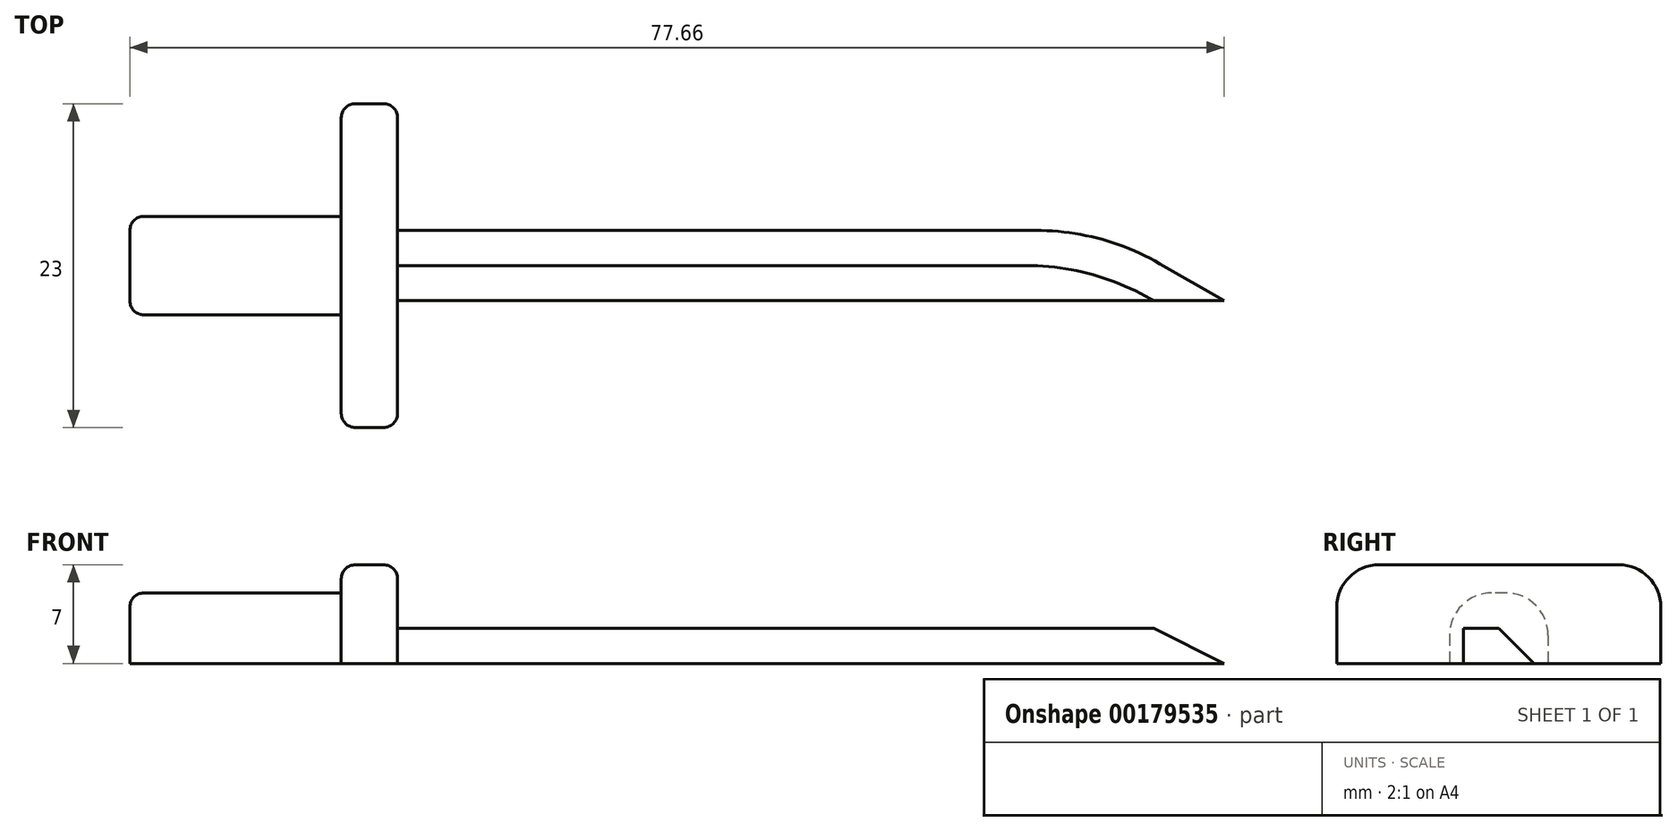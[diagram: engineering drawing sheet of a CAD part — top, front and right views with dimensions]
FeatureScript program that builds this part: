
annotation { "Feature Type Name" : "Feature", "Feature Type Description" : "" }
export const myFeature = defineFeature(function(context is Context, id is Id, definition is map)
    precondition{}
    {
        {
            var Q0;
            Q0=qCreatedBy(makeId("Top.planeOp"),FACE);
            var sketch = newSketch(context, id + "F0", { "sketchPlane" : qUnion([Q0])});
            skLineSegment(sketch, "E0.bottom", {"start": v(0, 0) * mm, "end": v(50, 0) * mm});
            skLineSegment(sketch, "E0.top", {"start": v(0, -5) * mm, "end": v(50, -5) * mm});
            skLineSegment(sketch, "E0.left", {"start": v(0, 0) * mm, "end": v(0, -5) * mm});
            skLineSegment(sketch, "E0.right", {"start": v(50, 0) * mm, "end": v(50, -5) * mm});
            skLineSegment(sketch, "E1", {"start": v(50, 0) * mm, "end": v(58.66, -5) * mm});
            skLineSegment(sketch, "E2", {"start": v(58.66, -5) * mm, "end": v(50, -5) * mm});
            skLineSegment(sketch, "E3.bottom", {"start": v(-4, 9) * mm, "end": v(0, 9) * mm});
            skLineSegment(sketch, "E3.top", {"start": v(-4, -14) * mm, "end": v(0, -14) * mm});
            skLineSegment(sketch, "E3.left", {"start": v(-4, 9) * mm, "end": v(-4, -14) * mm});
            skLineSegment(sketch, "E3.right", {"start": v(0, 9) * mm, "end": v(0, -14) * mm});
            skLineSegment(sketch, "E4.bottom", {"start": v(-19, 1) * mm, "end": v(-4, 1) * mm});
            skLineSegment(sketch, "E4.top", {"start": v(-19, -6) * mm, "end": v(-4, -6) * mm});
            skLineSegment(sketch, "E4.left", {"start": v(-19, 1) * mm, "end": v(-19, -6) * mm});
            skLineSegment(sketch, "E4.right", {"start": v(-4, 1) * mm, "end": v(-4, -6) * mm});
            skSolve(sketch);
        }
        {
            var Q0;
            {var subQ0=sQuery(id+"F0.wireOp",EDGE,"E0.bottom");Q0=makeQuery(id+"F0.imprint","IMPRINT",FACE,{"disambiguationData":[TD([[makeQuery(id+"F0.imprint","IMPRINT",EDGE,{"derivedFrom":subQ0}),-1.0]])]});}
            var Q1;
            Q1=makeQuery(id+"F0.imprint","IMPRINT",FACE,{"disambiguationData":[TD([[makeQuery(id+"F0.imprint","IMPRINT",EDGE,{"derivedFrom":sQuery(id+"F0.wireOp",EDGE,"E0.right")}),1.0]])]});
            extrude(context, id + "F1", {"entities" : qUnion([Q0, Q1]), "depth" : 2.5 * mm});
        }
        {
            var Q0;
            Q0=makeQuery(id+"F0.imprint","IMPRINT",FACE,{"disambiguationData":[TD([[makeQuery(id+"F0.imprint","IMPRINT",EDGE,{"derivedFrom":sQuery(id+"F0.wireOp",EDGE,"E4.bottom")}),-1.0]])]});
            extrude(context, id + "F2", {"entities" : qUnion([Q0]), "depth" : 5 * mm});
        }
        {
            var Q0;
            {var subQ3=sQuery(id+"F0.wireOp",EDGE,"E3.bottom");Q0=makeQuery(id+"F0.imprint","IMPRINT",FACE,{"disambiguationData":[TD([[makeQuery(id+"F0.imprint","IMPRINT",EDGE,{"derivedFrom":subQ3}),-1.0]])]});}
            extrude(context, id + "F3", {"entities" : qUnion([Q0]), "depth" : 7 * mm});
        }
        {
            var Q0;
            Q0=makeQuery(id+"F1.opExtrude","CAP_EDGE",EDGE,{"disambiguationData":[OSD([sQuery(id+"F0.wireOp",EDGE,"E0.bottom")])],"isStart":false});
            var Q1;
            Q1=makeQuery(id+"F1.opExtrude","CAP_EDGE",EDGE,{"disambiguationData":[OSD([sQuery(id+"F0.wireOp",EDGE,"E1")])],"isStart":false});
            chamfer(context, id + "F4", {"entities" : qUnion([Q0, Q1]), "width" : 2.5 * mm, "tangentPropagation" : true});
        }
        {
            var Q0;
            Q0=makeQuery(id+"F2.opExtrude","CAP_EDGE",EDGE,{"disambiguationData":[OSD([sQuery(id+"F0.wireOp",EDGE,"E4.bottom")])],"isStart":false});
            var Q1;
            Q1=makeQuery(id+"F2.opExtrude","CAP_EDGE",EDGE,{"disambiguationData":[OSD([sQuery(id+"F0.wireOp",EDGE,"E4.top")])],"isStart":false});
            var Q2;
            Q2=makeQuery(id+"F3.opExtrude","CAP_EDGE",EDGE,{"disambiguationData":[OSD([sQuery(id+"F0.wireOp",EDGE,"E3.bottom")])],"isStart":false});
            var Q3;
            Q3=makeQuery(id+"F3.opExtrude","CAP_EDGE",EDGE,{"disambiguationData":[OSD([sQuery(id+"F0.wireOp",EDGE,"E3.top")])],"isStart":false});
            fillet(context, id + "F5", {"entities" : qUnion([Q0, Q1, Q2, Q3]), "radius" : 3 * mm, "tangentPropagation" : true, "allowEdgeOverflow" : false});
        }
        {
            var Q0;
            Q0=makeQuery(id+"F5.opFillet","BLEND_EDGE",EDGE,{"blendedFrom":[makeQuery(id+"F2.opExtrude","CAP_EDGE",EDGE,{"disambiguationData":[OSD([sQuery(id+"F0.wireOp",EDGE,"E4.bottom")])],"isStart":false}),makeQuery(id+"F2.opExtrude","SWEPT_FACE",FACE,{"disambiguationData":[OSD([sQuery(id+"F0.wireOp",EDGE,"E4.left")])]})],"blendedInto":[makeQuery(id+"F2.opExtrude","SWEPT_FACE",FACE,{"disambiguationData":[OSD([sQuery(id+"F0.wireOp",EDGE,"E4.left")])]})]});
            var Q1;
            Q1=makeQuery(id+"F3.opExtrude","CAP_EDGE",EDGE,{"disambiguationData":[OSD([sQuery(id+"F0.wireOp",EDGE,"E3.left"),sQuery(id+"F0.wireOp",EDGE,"E4.right")])],"isStart":false});
            var Q2;
            Q2=makeQuery(id+"F3.opExtrude","CAP_EDGE",EDGE,{"disambiguationData":[OSD([sQuery(id+"F0.wireOp",EDGE,"E3.right")])],"isStart":false});
            fillet(context, id + "F6", {"entities" : qUnion([Q0, Q1, Q2]), "radius" : 1 * mm, "tangentPropagation" : true, "allowEdgeOverflow" : false});
        }
        {
            var Q0;
            Q0=makeQuery(id+"F4.opChamfer","BLEND_EDGE",EDGE,{"blendedFrom":[makeQuery(id+"F1.opExtrude","CAP_EDGE",EDGE,{"disambiguationData":[OSD([sQuery(id+"F0.wireOp",EDGE,"E0.bottom")])],"isStart":false}),makeQuery(id+"F1.opExtrude","CAP_EDGE",EDGE,{"disambiguationData":[OSD([sQuery(id+"F0.wireOp",EDGE,"E1")])],"isStart":false})],"blendedInto":[]});
            fillet(context, id + "F7", {"entities" : qUnion([Q0]), "radius" : 25 * mm, "tangentPropagation" : true, "allowEdgeOverflow" : false});
        }
    });
